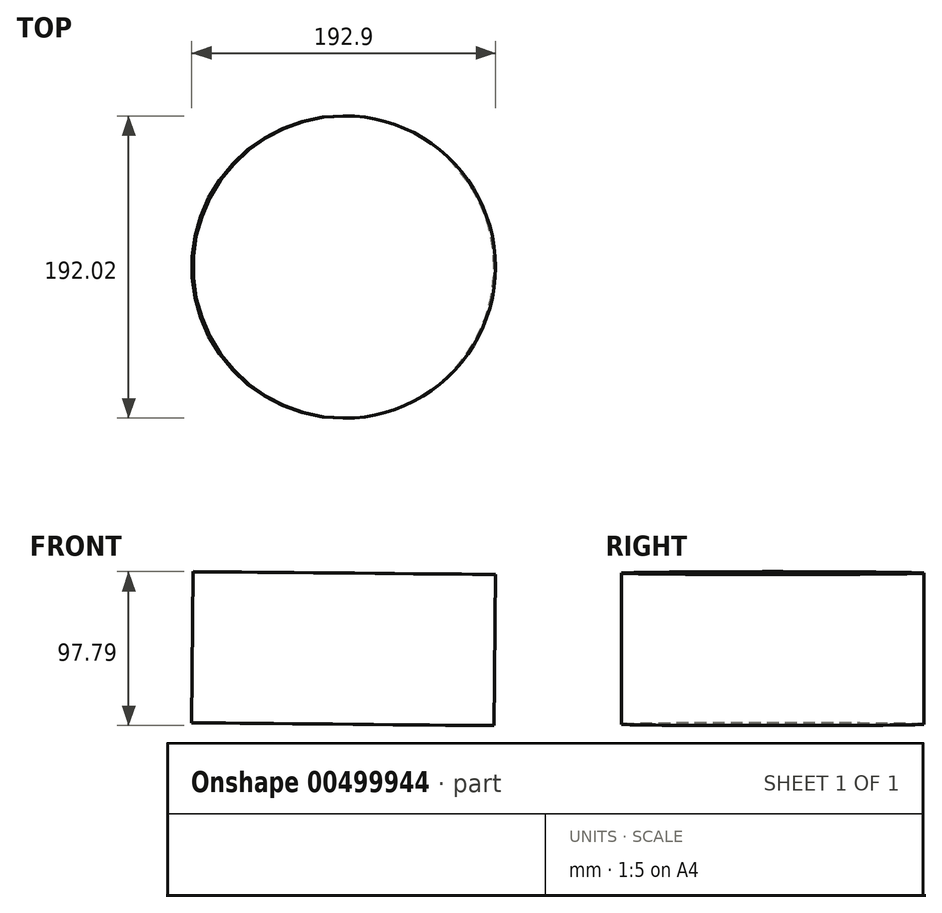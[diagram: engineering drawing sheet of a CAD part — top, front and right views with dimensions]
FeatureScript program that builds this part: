
annotation { "Feature Type Name" : "Feature", "Feature Type Description" : "" }
export const myFeature = defineFeature(function(context is Context, id is Id, definition is map)
    precondition{}
    {
        {
            var Q0;
            Q0=qCreatedBy(makeId("Front.planeOp"),FACE);
            var sketch = newSketch(context, id + "F0", { "sketchPlane" : qUnion([Q0])});
            skCircle(sketch, "E0.cCircle", {"center": v(0, 0) * mm, "radius": 67.89 * mm, "construction": true});
            skLineSegment(sketch, "E0.0", {"start": v(-47.56, 48.45) * mm, "end": v(48.45, 47.56) * mm});
            skLineSegment(sketch, "E0.1", {"start": v(48.45, 47.56) * mm, "end": v(47.56, -48.45) * mm});
            skLineSegment(sketch, "E0.2", {"start": v(47.56, -48.45) * mm, "end": v(-48.45, -47.56) * mm});
            skLineSegment(sketch, "E0.3", {"start": v(-48.45, -47.56) * mm, "end": v(-47.56, 48.45) * mm});
            skSolve(sketch);
        }
        {
            var Q0;
            Q0=makeQuery(id+"F0.imprint","IMPRINT",FACE,{"disambiguationData":[TD([[makeQuery(id+"F0.imprint","IMPRINT",EDGE,{"derivedFrom":sQuery(id+"F0.wireOp",EDGE,"E0.0")}),-1.0]])]});
            var Q1;
            Q1=sQuery(id+"F0.wireOp",EDGE,"E0.1");
            revolve(context, id + "F1", {"entities" : qUnion([Q0]), "axis" : qUnion([Q1]), "revolveType" : RevolveType.FULL});
        }
    });
